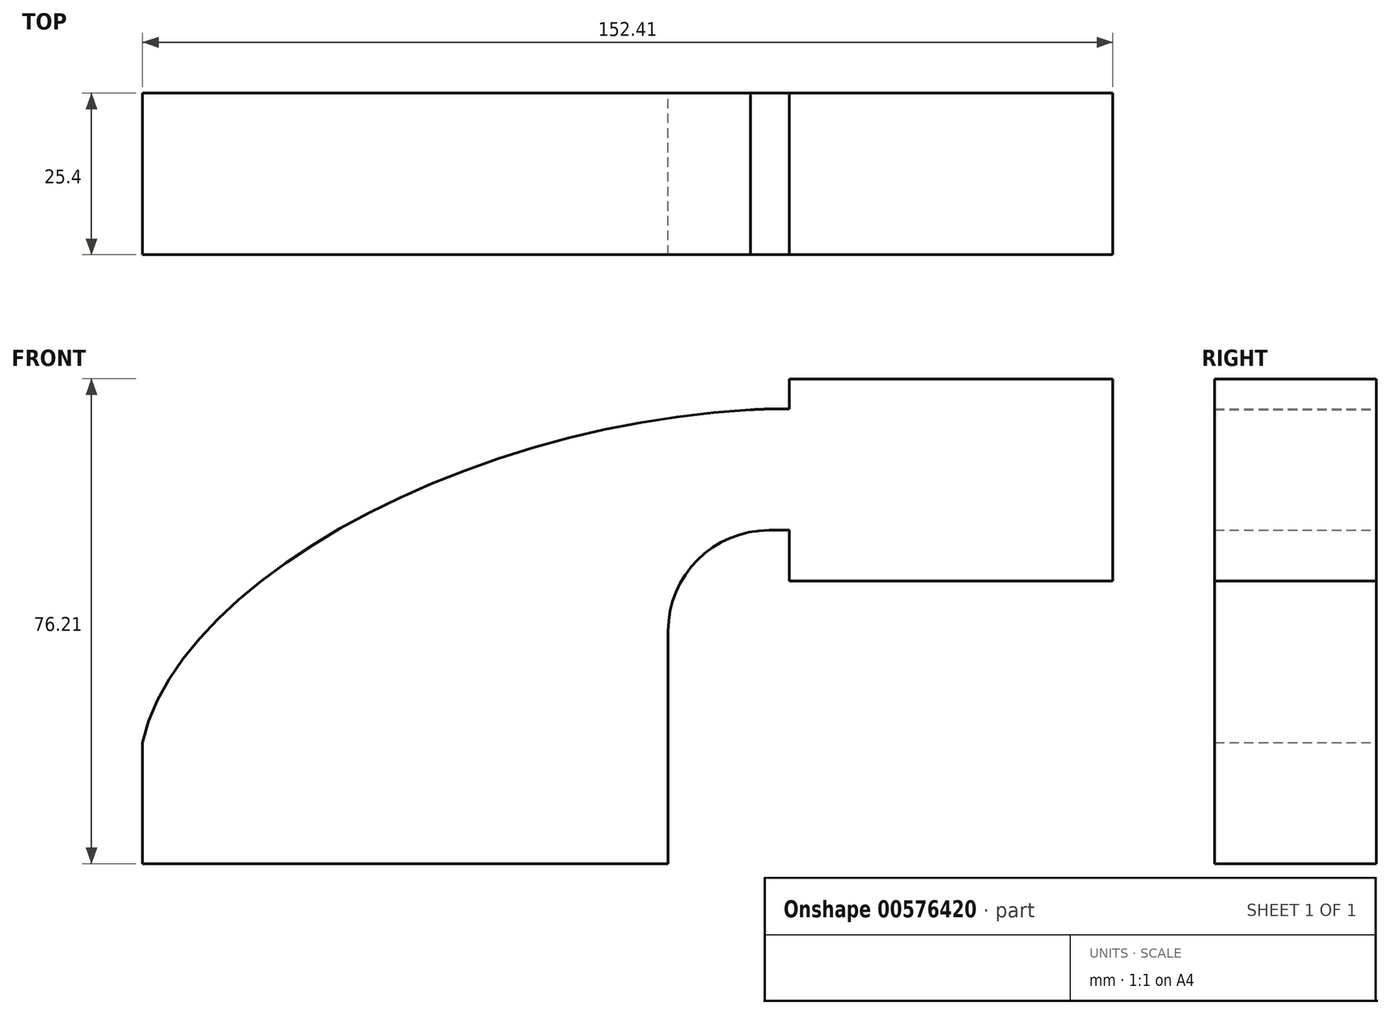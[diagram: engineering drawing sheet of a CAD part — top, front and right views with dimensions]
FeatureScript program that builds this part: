
annotation { "Feature Type Name" : "Feature", "Feature Type Description" : "" }
export const myFeature = defineFeature(function(context is Context, id is Id, definition is map)
    precondition{}
    {
        {
            var Q0;
            Q0=qCreatedBy(makeId("Front.planeOp"),FACE);
            var sketch = newSketch(context, id + "F0", { "sketchPlane" : qUnion([Q0])});
            skLineSegment(sketch, "E0.bottom", {"start": v(-41.28, -9.52) * mm, "end": v(41.28, -9.52) * mm});
            skLineSegment(sketch, "E0.top", {"start": v(-41.28, 9.53) * mm, "end": v(41.28, 9.53) * mm});
            skLineSegment(sketch, "E0.left", {"start": v(-41.28, -9.52) * mm, "end": v(-41.28, 9.53) * mm});
            skLineSegment(sketch, "E0.right", {"start": v(41.28, -9.52) * mm, "end": v(41.28, 9.53) * mm});
            skPoint(sketch, "E0.middle", {"position": v(0, 0) * mm});
            skLineSegment(sketch, "E1.bottom", {"start": v(111.13, 34.93) * mm, "end": v(60.33, 34.93) * mm});
            skLineSegment(sketch, "E1.top", {"start": v(111.13, 66.68) * mm, "end": v(60.33, 66.68) * mm});
            skLineSegment(sketch, "E1.left", {"start": v(111.13, 34.93) * mm, "end": v(111.13, 66.68) * mm});
            skLineSegment(sketch, "E1.right", {"start": v(60.33, 34.93) * mm, "end": v(60.33, 66.68) * mm});
            skPoint(sketch, "E1.middle", {"position": v(85.73, 50.8) * mm});
            skLineSegment(sketch, "E2", {"start": v(41.27, 9.52) * mm, "end": v(41.27, 9.52) * mm});
            skLineSegment(sketch, "E3", {"start": v(85.73, 42.88) * mm, "end": v(57.15, 42.88) * mm});
            skLineSegment(sketch, "E4", {"start": v(41.28, 9.53) * mm, "end": v(41.28, 27) * mm});
            skArc(sketch, "E5", {"start": v(41.27, 27) * mm, "mid": v(45.92, 38.23) * mm, "end": v(57.15, 42.88) * mm});
            skLineSegment(sketch, "E6.0", {"start": v(85.73, 61.93) * mm, "end": v(57.15, 61.93) * mm});
            skArc(sketch, "E6.1", {"start": v(22.22, 27) * mm, "mid": v(32.45, 51.7) * mm, "end": v(57.15, 61.93) * mm});
            skLineSegment(sketch, "E6.2", {"start": v(22.22, 9.53) * mm, "end": v(22.22, 27) * mm});
            skLineSegment(sketch, "E7", {"start": v(85.73, 42.88) * mm, "end": v(85.73, 61.93) * mm});
            skLineSegment(sketch, "E8", {"start": v(41.28, 9.53) * mm, "end": v(22.22, 9.53) * mm});
            skFitSpline(sketch, "E9", {"points": [v(-41.27, 9.53) * mm, v(57.15, 61.93) * mm], "startDerivative": vector(17.29, 78.62) * mm, "endDerivative": vector(135.22, 4.24) * mm});
            skSolve(sketch);
        }
        {
            var Q0;
            Q0 = qSketchRegion(id + "F0", true);
            extrude(context, id + "F1", {"entities" : qUnion([Q0]), "depth" : 25.4 * mm, "offsetDistance" : 25.4 * mm});
        }
    });
